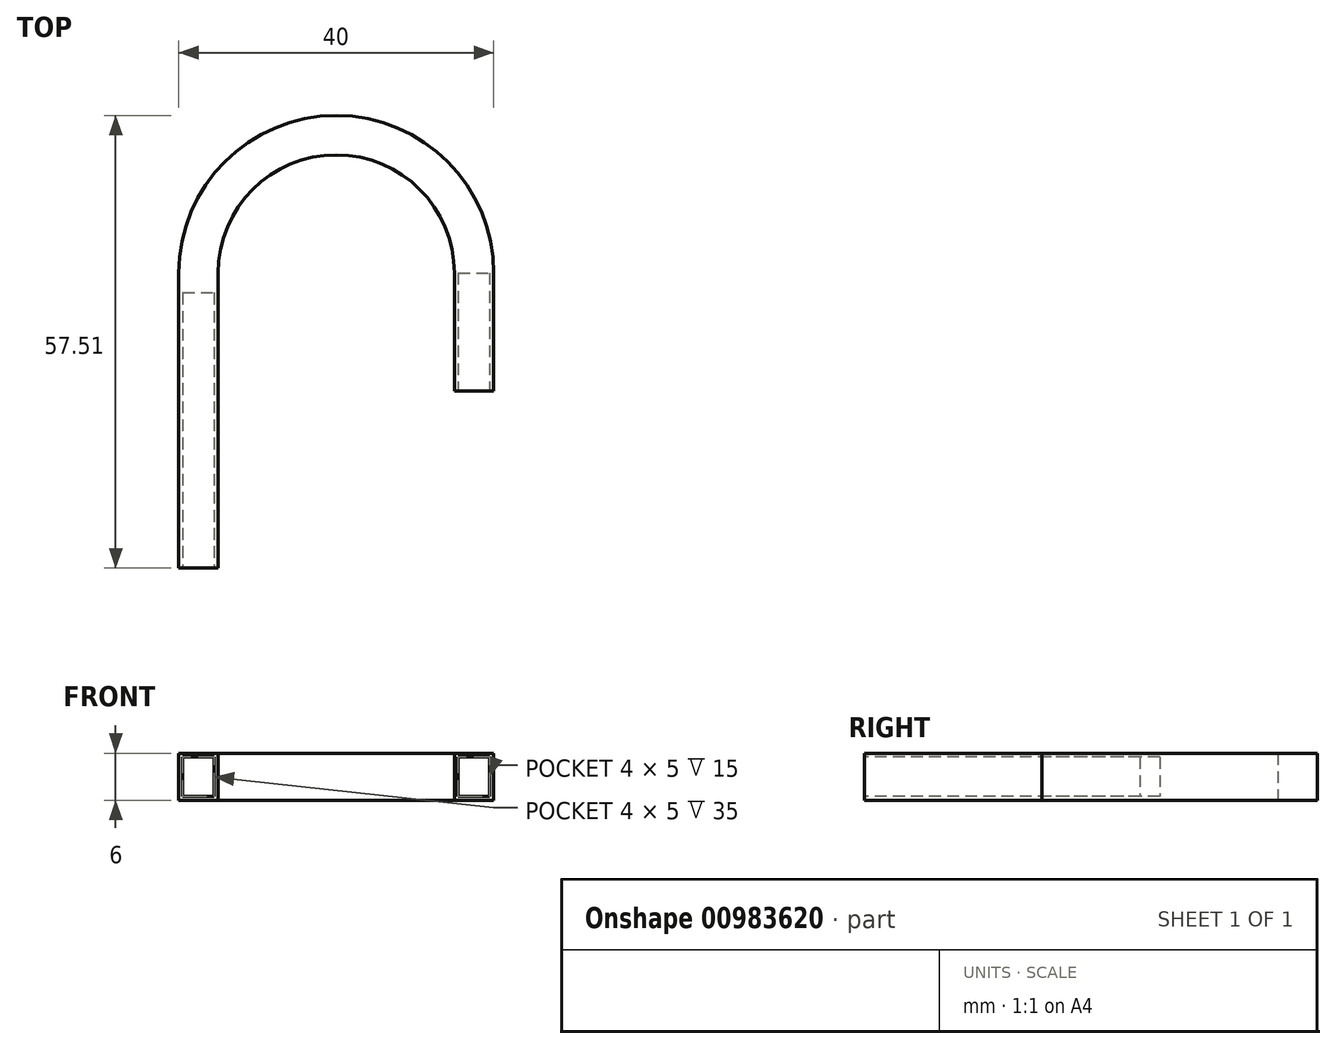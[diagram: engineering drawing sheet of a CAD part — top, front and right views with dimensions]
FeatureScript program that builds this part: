
annotation { "Feature Type Name" : "Feature", "Feature Type Description" : "" }
export const myFeature = defineFeature(function(context is Context, id is Id, definition is map)
    precondition{}
    {
        {
            var Q0;
            Q0=qCreatedBy(makeId("Top.planeOp"),FACE);
            var sketch = newSketch(context, id + "F0", { "sketchPlane" : qUnion([Q0])});
            skArc(sketch, "E0", {"start": v(15, 0) * mm, "mid": v(0, 15) * mm, "end": v(-15, 0) * mm});
            skLineSegment(sketch, "E1", {"start": v(15, 0) * mm, "end": v(15, -15) * mm});
            skLineSegment(sketch, "E2", {"start": v(-15, 0) * mm, "end": v(-15, -37.51) * mm});
            skPoint(sketch, "E3.start.orphan", {"position": v(0, -15) * mm});
            skArc(sketch, "E4.0", {"start": v(20, 0) * mm, "mid": v(0, 20) * mm, "end": v(-20, 0) * mm});
            skLineSegment(sketch, "E5", {"start": v(20, 0) * mm, "end": v(20, -15) * mm});
            skLineSegment(sketch, "E6", {"start": v(20, -15) * mm, "end": v(15, -15) * mm});
            skLineSegment(sketch, "E7", {"start": v(-20, 0) * mm, "end": v(-20, -37.51) * mm});
            skLineSegment(sketch, "E8", {"start": v(-20, -37.51) * mm, "end": v(-15, -37.51) * mm});
            skSolve(sketch);
        }
        {
            var Q0;
            Q0=makeQuery(id+"F0.imprint","IMPRINT",FACE,{"disambiguationData":[TD([[makeQuery(id+"F0.imprint","IMPRINT",EDGE,{"derivedFrom":sQuery(id+"F0.wireOp",EDGE,"E0")}),-1.0]])]});
            extrude(context, id + "F1", {"entities" : qUnion([Q0]), "depth" : 6 * mm, "offsetDistance" : 25 * mm});
        }
        {
            var Q0;
            Q0=makeQuery(id+"F1.opExtrude","SWEPT_FACE",FACE,{"disambiguationData":[OSD([sQuery(id+"F0.wireOp",EDGE,"E6")])]});
            var sketch = newSketch(context, id + "F2", { "sketchPlane" : qUnion([Q0])});
            skLineSegment(sketch, "E9", {"start": v(17.5, 6) * mm, "end": v(17.5, 5.5) * mm, "construction": true});
            skLineSegment(sketch, "E10", {"start": v(15, 3) * mm, "end": v(15.5, 3) * mm, "construction": true});
            skLineSegment(sketch, "E11", {"start": v(17.5, 0) * mm, "end": v(17.5, 0.5) * mm, "construction": true});
            skLineSegment(sketch, "E12", {"start": v(20, 3) * mm, "end": v(19.5, 3) * mm, "construction": true});
            skLineSegment(sketch, "E13.bottom", {"start": v(15.5, 5.5) * mm, "end": v(19.5, 5.5) * mm});
            skLineSegment(sketch, "E13.top", {"start": v(15.5, 0.5) * mm, "end": v(19.5, 0.5) * mm});
            skLineSegment(sketch, "E13.left", {"start": v(15.5, 5.5) * mm, "end": v(15.5, 0.5) * mm});
            skLineSegment(sketch, "E13.right", {"start": v(19.5, 5.5) * mm, "end": v(19.5, 0.5) * mm});
            skSolve(sketch);
        }
        {
            var Q0;
            Q0=makeQuery(id+"F2.imprint","IMPRINT",FACE,{"disambiguationData":[TD([[makeQuery(id+"F2.imprint","IMPRINT",EDGE,{"derivedFrom":sQuery(id+"F2.wireOp",EDGE,"E13.bottom")}),-1.0]])]});
            extrude(context, id + "F3", {"entities" : qUnion([Q0]), "operationType" : NewBodyOperationType.REMOVE, "oppositeDirection" : true, "depth" : 15 * mm, "offsetDistance" : 25 * mm});
        }
        {
            var Q0;
            Q0=makeQuery(id+"F1.opExtrude","SWEPT_FACE",FACE,{"disambiguationData":[OSD([sQuery(id+"F0.wireOp",EDGE,"E8")])]});
            var sketch = newSketch(context, id + "F4", { "sketchPlane" : qUnion([Q0])});
            skLineSegment(sketch, "E14", {"start": v(-20, 3) * mm, "end": v(-19.5, 3) * mm, "construction": true});
            skLineSegment(sketch, "E15", {"start": v(-17.5, 6) * mm, "end": v(-17.5, 5.5) * mm, "construction": true});
            skLineSegment(sketch, "E16", {"start": v(-15, 3) * mm, "end": v(-15.5, 3) * mm, "construction": true});
            skLineSegment(sketch, "E17", {"start": v(-17.5, 0) * mm, "end": v(-17.5, 0.5) * mm, "construction": true});
            skLineSegment(sketch, "E18.bottom", {"start": v(-19.5, 5.5) * mm, "end": v(-15.5, 5.5) * mm});
            skLineSegment(sketch, "E18.top", {"start": v(-19.5, 0.5) * mm, "end": v(-15.5, 0.5) * mm});
            skLineSegment(sketch, "E18.left", {"start": v(-19.5, 5.5) * mm, "end": v(-19.5, 0.5) * mm});
            skLineSegment(sketch, "E18.right", {"start": v(-15.5, 5.5) * mm, "end": v(-15.5, 0.5) * mm});
            skSolve(sketch);
        }
        {
            var Q0;
            Q0=makeQuery(id+"F4.imprint","IMPRINT",FACE,{"disambiguationData":[TD([[makeQuery(id+"F4.imprint","IMPRINT",EDGE,{"derivedFrom":sQuery(id+"F4.wireOp",EDGE,"E18.bottom")}),-1.0]])]});
            extrude(context, id + "F5", {"entities" : qUnion([Q0]), "operationType" : NewBodyOperationType.REMOVE, "oppositeDirection" : true, "depth" : 35 * mm, "offsetDistance" : 25 * mm});
        }
    });
